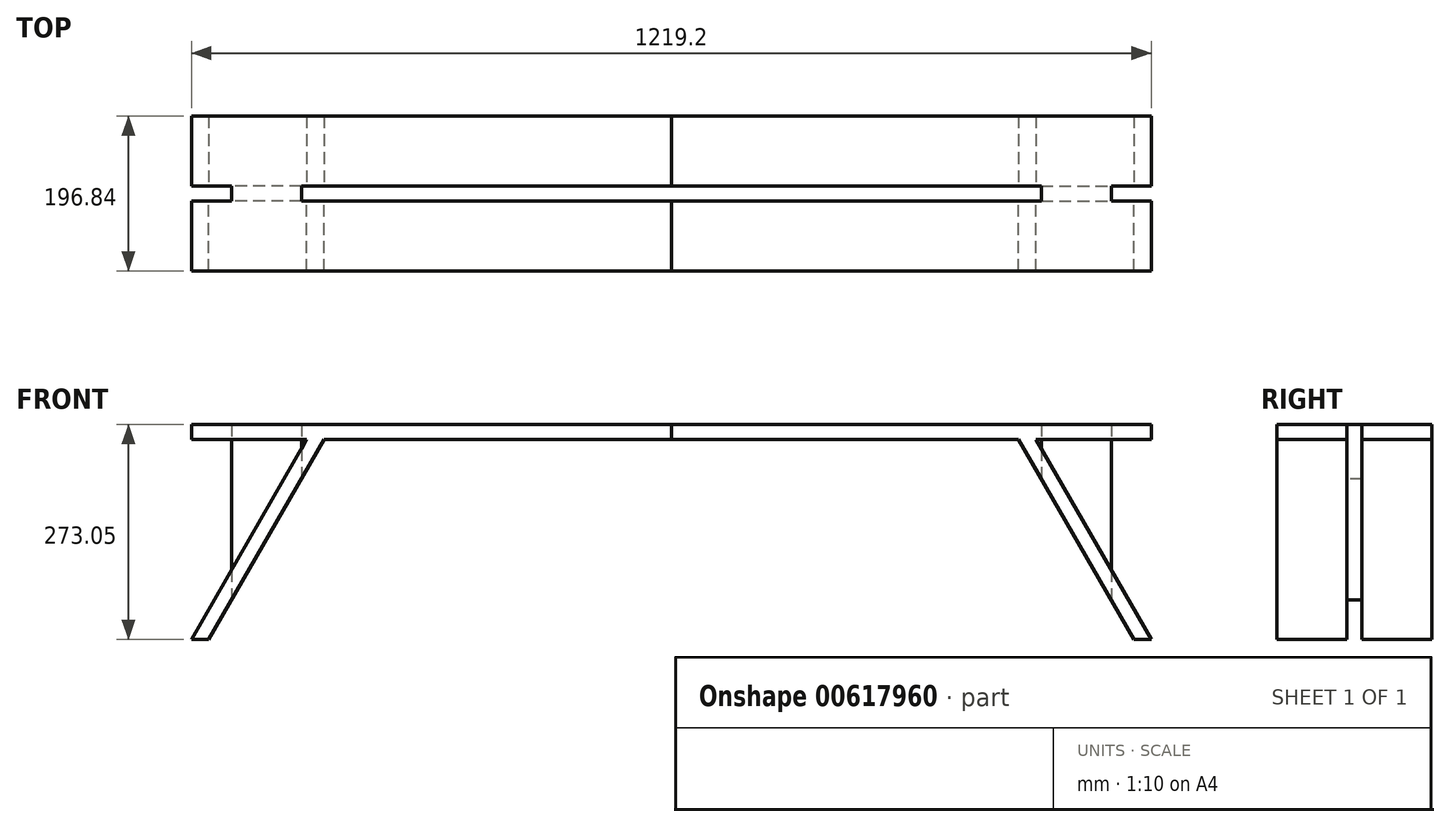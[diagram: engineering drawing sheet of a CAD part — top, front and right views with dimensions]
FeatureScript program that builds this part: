
annotation { "Feature Type Name" : "Feature", "Feature Type Description" : "" }
export const myFeature = defineFeature(function(context is Context, id is Id, definition is map)
    precondition{}
    {
        {
            var Q0;
            Q0=qCreatedBy(makeId("Top.planeOp"),FACE);
            var sketch = newSketch(context, id + "F0", { "sketchPlane" : qUnion([Q0])});
            skLineSegment(sketch, "E0.bottom", {"start": v(0, -9.53) * mm, "end": v(609.6, -9.52) * mm});
            skLineSegment(sketch, "E0.top", {"start": v(0, -98.43) * mm, "end": v(609.6, -98.42) * mm});
            skLineSegment(sketch, "E0.left", {"start": v(0, -9.53) * mm, "end": v(0, -98.43) * mm});
            skLineSegment(sketch, "E0.right", {"start": v(609.6, -9.52) * mm, "end": v(609.6, -98.42) * mm});
            skSolve(sketch);
        }
        {
            var Q0;
            Q0 = qSketchRegion(id + "F0", true);
            extrude(context, id + "F1", {"entities" : qUnion([Q0]), "depth" : 19.05 * mm, "offsetDistance" : 25.4 * mm});
        }
        {
            var Q0;
            Q0=qCreatedBy(makeId("Front.planeOp"),FACE);
            var sketch = newSketch(context, id + "F2", { "sketchPlane" : qUnion([Q0])});
            skLineSegment(sketch, "E1.bottom", {"start": v(609.6, 0) * mm, "end": v(406.4, 0) * mm, "construction": true});
            skLineSegment(sketch, "E1.top", {"start": v(609.6, -254) * mm, "end": v(406.4, -254) * mm, "construction": true});
            skLineSegment(sketch, "E1.left", {"start": v(609.6, 0) * mm, "end": v(609.6, -254) * mm, "construction": true});
            skLineSegment(sketch, "E1.right", {"start": v(406.4, 0) * mm, "end": v(406.4, -254) * mm, "construction": true});
            skLineSegment(sketch, "E2.bottom", {"start": v(440.96, 0) * mm, "end": v(457.45, 9.52) * mm});
            skLineSegment(sketch, "E2.top", {"start": v(593.1, -263.53) * mm, "end": v(609.6, -254) * mm});
            skLineSegment(sketch, "E2.left", {"start": v(440.96, 0) * mm, "end": v(593.1, -263.53) * mm});
            skLineSegment(sketch, "E2.right", {"start": v(457.45, 9.53) * mm, "end": v(609.6, -254) * mm});
            skLineSegment(sketch, "E3.bottom", {"start": v(469.9, 19.05) * mm, "end": v(558.8, 19.05) * mm});
            skLineSegment(sketch, "E3.top", {"start": v(469.9, -269.99) * mm, "end": v(558.8, -269.99) * mm});
            skLineSegment(sketch, "E3.left", {"start": v(469.9, 19.05) * mm, "end": v(469.9, -269.99) * mm});
            skLineSegment(sketch, "E3.right", {"start": v(558.8, 19.05) * mm, "end": v(558.8, -269.99) * mm});
            skSolve(sketch);
        }
        {
            var Q0;
            Q0=makeQuery(id+"F1.opExtrude","SWEPT_FACE",FACE,{"disambiguationData":[OSD([sQuery(id+"F0.wireOp",EDGE,"E0.bottom")])]});
            var sketch = newSketch(context, id + "F3", { "sketchPlane" : qUnion([Q0])});
            skLineSegment(sketch, "E4.0", {"start": v(-440.96, 0) * mm, "end": v(-587.6, -254) * mm});
            skLineSegment(sketch, "E5.0", {"start": v(-462.95, 0) * mm, "end": v(-609.6, -254) * mm});
            skLineSegment(sketch, "E6.0", {"start": v(-609.6, -254) * mm, "end": v(-587.6, -254) * mm});
            skLineSegment(sketch, "E7.0", {"start": v(-462.95, 0) * mm, "end": v(-440.96, 0) * mm});
            skPoint(sketch, "E8.orphan", {"position": v(-406.4, 0) * mm});
            skPoint(sketch, "E9.orphan", {"position": v(-609.6, 0) * mm});
            skPoint(sketch, "E10.orphan", {"position": v(-406.4, -254) * mm});
            skPoint(sketch, "E11.orphan", {"position": v(-457.45, 9.53) * mm});
            skSolve(sketch);
        }
        {
            var Q0;
            Q0 = qSketchRegion(id + "F3", true);
            extrude(context, id + "F4", {"entities" : qUnion([Q0]), "oppositeDirection" : true, "depth" : 88.9 * mm, "offsetDistance" : 25.4 * mm});
        }
        {
            var Q0;
            Q0=makeQuery(id+"F1.opExtrude","SWEPT_FACE",FACE,{"disambiguationData":[OSD([sQuery(id+"F0.wireOp",EDGE,"E0.bottom")])]});
            var sketch = newSketch(context, id + "F5", { "sketchPlane" : qUnion([Q0])});
            skLineSegment(sketch, "E12.0", {"start": v(-469.9, 19.05) * mm, "end": v(-558.8, 19.05) * mm});
            skLineSegment(sketch, "E13.0", {"start": v(-558.8, 19.05) * mm, "end": v(-558.8, -204.11) * mm});
            skLineSegment(sketch, "E14.0", {"start": v(-469.9, 19.05) * mm, "end": v(-469.9, -50.13) * mm});
            skLineSegment(sketch, "E15.0", {"start": v(-469.9, -50.13) * mm, "end": v(-558.8, -204.11) * mm});
            skSolve(sketch);
        }
        {
            var Q0;
            Q0 = qSketchRegion(id + "F5", true);
            extrude(context, id + "F6", {"entities" : qUnion([Q0]), "depth" : 19.05 * mm, "offsetDistance" : 25.4 * mm});
        }
        {
            var Q0;
            Q0=makeQuery(id+"F4.opExtrude","SWEPT_BODY",BODY,{"disambiguationData":[OSD([sQuery(id+"F3.wireOp",EDGE,"E4.0"),sQuery(id+"F3.wireOp",EDGE,"E5.0"),sQuery(id+"F3.wireOp",EDGE,"E6.0"),sQuery(id+"F3.wireOp",EDGE,"E7.0")])]});
            var Q1;
            Q1=qCreatedBy(makeId("Front.planeOp"),FACE);
            mirror(context, id + "F7", {"entities" : qUnion([Q0]), "mirrorPlane" : qUnion([Q1])});
        }
        {
            var Q0;
            Q0=makeQuery(id+"F1.opExtrude","SWEPT_BODY",BODY,{"disambiguationData":[OSD([sQuery(id+"F0.wireOp",EDGE,"E0.bottom"),sQuery(id+"F0.wireOp",EDGE,"E0.top"),sQuery(id+"F0.wireOp",EDGE,"E0.left"),sQuery(id+"F0.wireOp",EDGE,"E0.right")])]});
            var Q1;
            Q1=qCreatedBy(makeId("Front.planeOp"),FACE);
            mirror(context, id + "F8", {"operationType" : NewBodyOperationType.ADD, "entities" : qUnion([Q0]), "mirrorPlane" : qUnion([Q1])});
        }
        {
            var Q0;
            Q0=makeQuery(id+"F4.opExtrude","SWEPT_BODY",BODY,{"disambiguationData":[OSD([sQuery(id+"F3.wireOp",EDGE,"E4.0"),sQuery(id+"F3.wireOp",EDGE,"E5.0"),sQuery(id+"F3.wireOp",EDGE,"E6.0"),sQuery(id+"F3.wireOp",EDGE,"E7.0")])]});
            var Q1;
            Q1=makeQuery(id+"F6.opExtrude","SWEPT_BODY",BODY,{"disambiguationData":[OSD([sQuery(id+"F5.wireOp",EDGE,"E12.0"),sQuery(id+"F5.wireOp",EDGE,"E13.0"),sQuery(id+"F5.wireOp",EDGE,"E14.0"),sQuery(id+"F5.wireOp",EDGE,"E15.0")])]});
            var Q2;
            Q2=makeQuery(id+"F7.opPattern","COPY",BODY,{"derivedFrom":makeQuery(id+"F4.opExtrude","SWEPT_BODY",BODY,{"disambiguationData":[OSD([sQuery(id+"F3.wireOp",EDGE,"E4.0"),sQuery(id+"F3.wireOp",EDGE,"E5.0"),sQuery(id+"F3.wireOp",EDGE,"E6.0"),sQuery(id+"F3.wireOp",EDGE,"E7.0")])]}),"instanceName":"1"});
            var Q3;
            Q3=qCreatedBy(makeId("Right.planeOp"),FACE);
            mirror(context, id + "F9", {"entities" : qUnion([Q0, Q1, Q2]), "mirrorPlane" : qUnion([Q3])});
        }
    });
